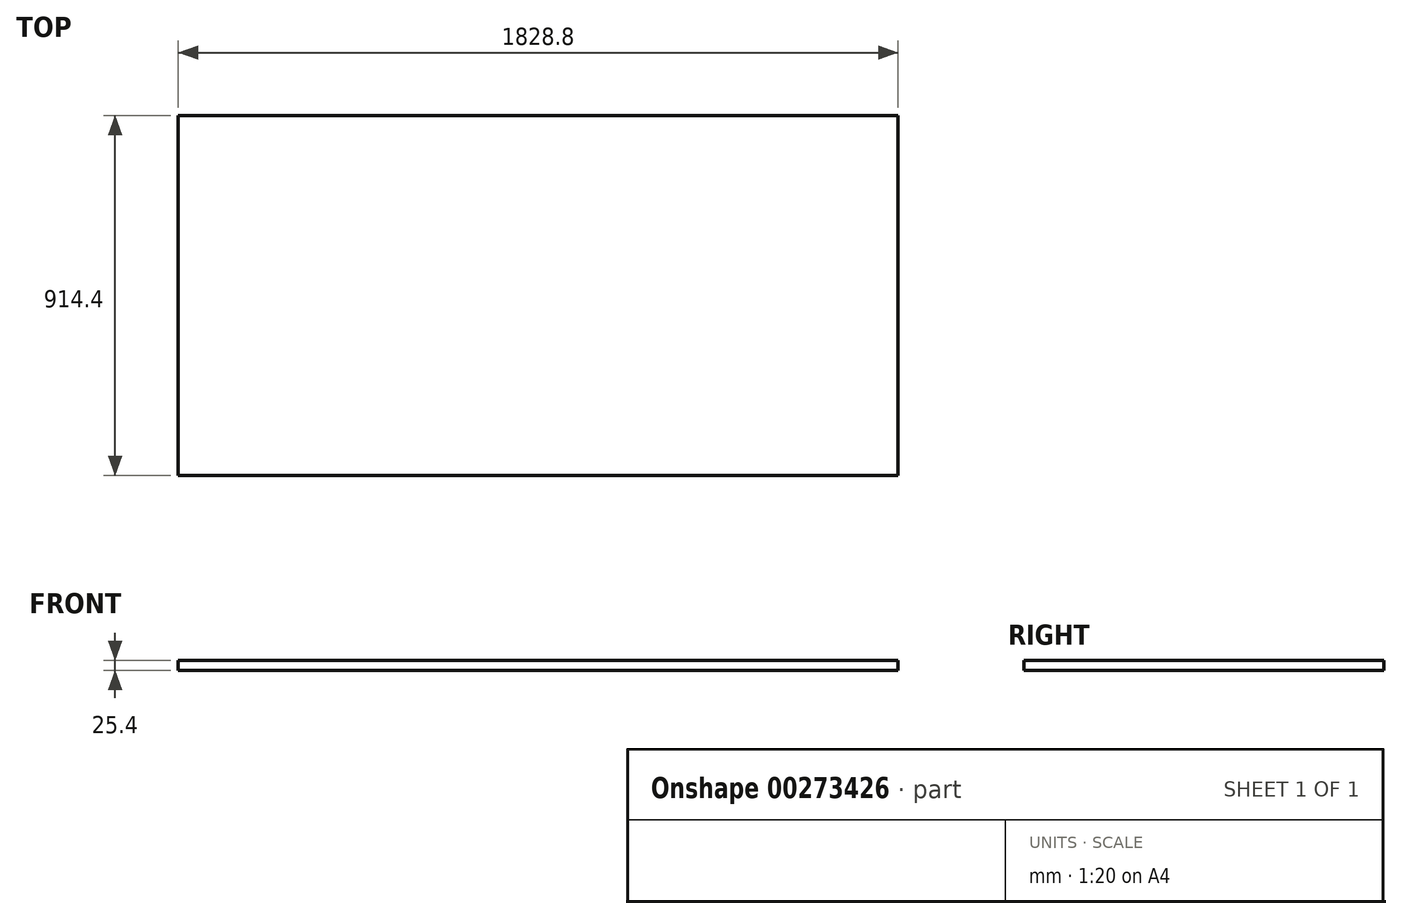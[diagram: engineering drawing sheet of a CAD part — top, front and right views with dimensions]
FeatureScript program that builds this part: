
annotation { "Feature Type Name" : "Feature", "Feature Type Description" : "" }
export const myFeature = defineFeature(function(context is Context, id is Id, definition is map)
    precondition{}
    {
        {
            var Q0;
            Q0=qCreatedBy(makeId("Top.planeOp"),FACE);
            var sketch = newSketch(context, id + "F0", { "sketchPlane" : qUnion([Q0])});
            skLineSegment(sketch, "E0.bottom", {"start": v(-607.6, 769.76) * mm, "end": v(1221.2, 769.76) * mm});
            skLineSegment(sketch, "E0.top", {"start": v(-607.6, -144.64) * mm, "end": v(1221.2, -144.64) * mm});
            skLineSegment(sketch, "E0.left", {"start": v(-607.6, 769.76) * mm, "end": v(-607.6, -144.64) * mm});
            skLineSegment(sketch, "E0.right", {"start": v(1221.2, 769.76) * mm, "end": v(1221.2, -144.64) * mm});
            skSolve(sketch);
        }
        {
            var Q0;
            Q0=makeQuery(id+"F0.imprint","IMPRINT",FACE,{"disambiguationData":[TD([[makeQuery(id+"F0.imprint","IMPRINT",EDGE,{"derivedFrom":sQuery(id+"F0.wireOp",EDGE,"E0.bottom")}),-1.0]])]});
            extrude(context, id + "F1", {"entities" : qUnion([Q0]), "depth" : 25.4 * mm});
        }
    });
